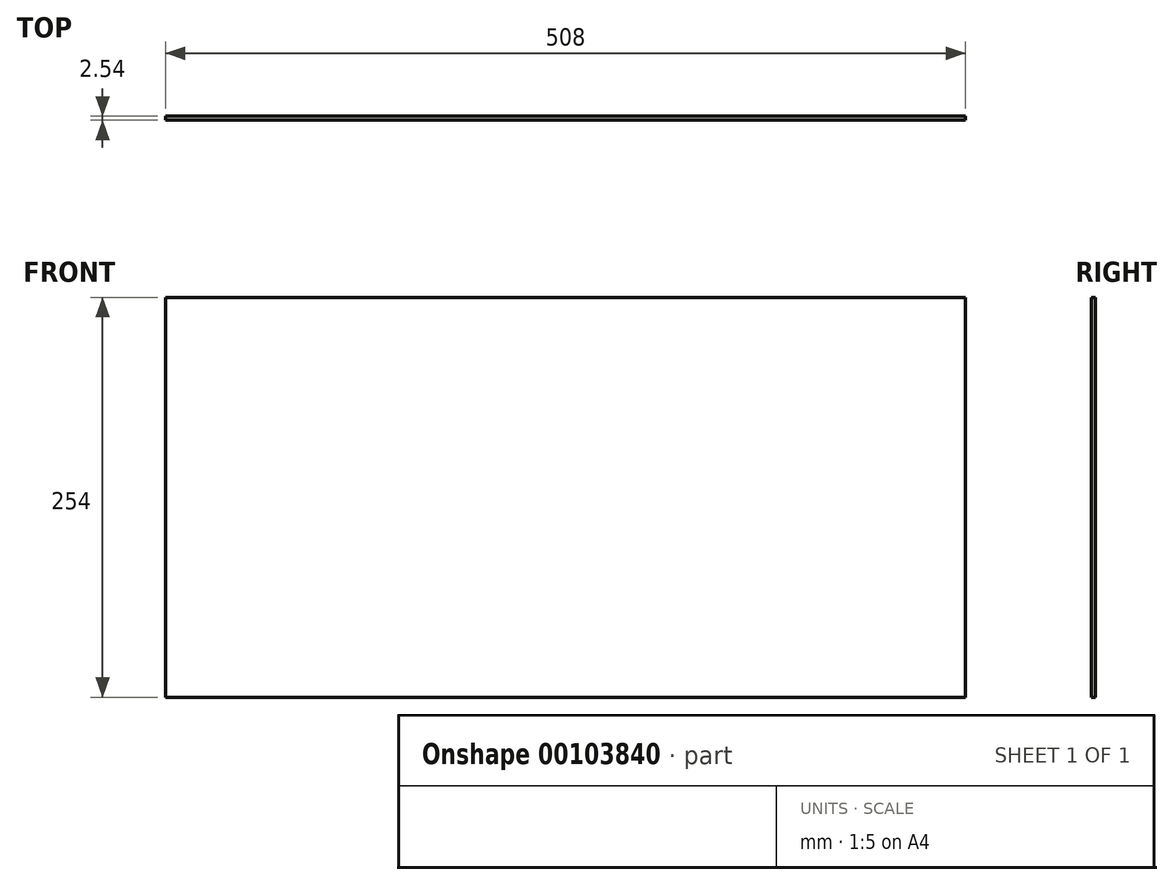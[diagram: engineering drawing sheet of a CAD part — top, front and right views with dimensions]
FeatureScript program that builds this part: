
annotation { "Feature Type Name" : "Feature", "Feature Type Description" : "" }
export const myFeature = defineFeature(function(context is Context, id is Id, definition is map)
    precondition{}
    {
        {
            var Q0;
            Q0=qCreatedBy(makeId("Front.planeOp"),FACE);
            var sketch = newSketch(context, id + "F0", { "sketchPlane" : qUnion([Q0])});
            skLineSegment(sketch, "E0.bottom", {"start": v(-254, 127) * mm, "end": v(254, 127) * mm});
            skLineSegment(sketch, "E0.top", {"start": v(-254, -127) * mm, "end": v(254, -127) * mm});
            skLineSegment(sketch, "E0.left", {"start": v(-254, 127) * mm, "end": v(-254, -127) * mm});
            skLineSegment(sketch, "E0.right", {"start": v(254, 127) * mm, "end": v(254, -127) * mm});
            skSolve(sketch);
        }
        {
            var Q0;
            Q0=makeQuery(id+"F0.imprint","IMPRINT",FACE,{"disambiguationData":[TD([[makeQuery(id+"F0.imprint","IMPRINT",EDGE,{"derivedFrom":sQuery(id+"F0.wireOp",EDGE,"E0.bottom")}),-1.0]])]});
            extrude(context, id + "F1", {"entities" : qUnion([Q0]), "depth" : 2.54 * mm});
        }
    });
